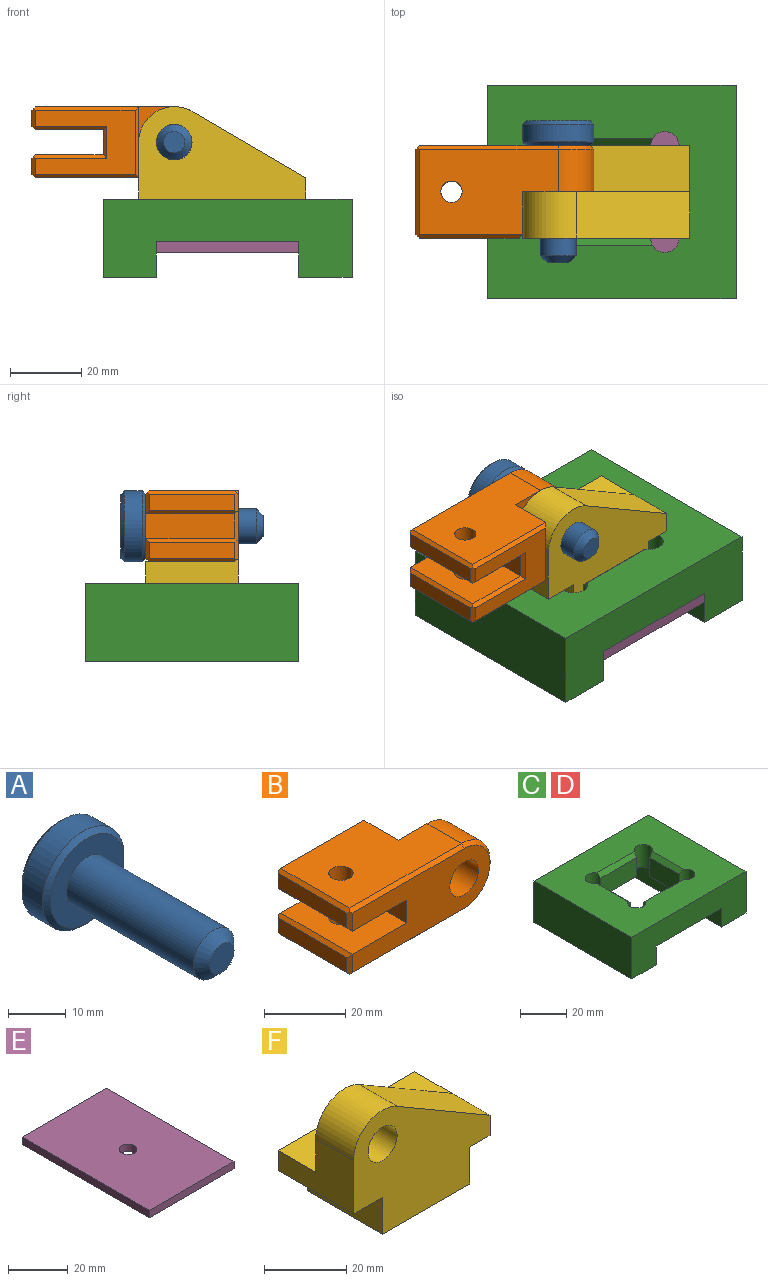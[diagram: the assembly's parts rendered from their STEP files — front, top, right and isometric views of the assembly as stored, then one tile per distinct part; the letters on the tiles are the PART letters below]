
ASSEMBLY  parts=6 mates=4
PART A: 8 faces, bbox 20x40x20 mm
  f0: cylinder r=10mm len=20mm, axis (0,1,0), area 314.2mm2, adj f5,f6
  f1: plane 18x18mm, normal (0,-1,0), area 175.9mm2, adj f3,f6
  f2: plane 18x18mm, normal (0,1,0), area 254.5mm2, adj f5
  f3: cylinder r=5mm len=31mm, axis (0,1,0), area 973.9mm2, adj f1,f7
  f4: plane 6x6mm, normal (0,-1,0), area 28.3mm2, adj f7
  f5: cone r=10mm half-angle=45deg, axis (0,-1,0), area 84.4mm2, adj f0,f2
  f6: cone r=9mm half-angle=45deg, axis (0,1,0), area 84.4mm2, adj f0,f1
  f7: cone r=3mm half-angle=45deg, axis (0,1,0), area 71.1mm2, adj f3,f4
PART B: 32 faces, bbox 50x26x20 mm
  f0: plane 39x24mm, normal (0,0,1), area 787.7mm2, adj f8,f12,f16,f21,f22,f23,f27
  f1: plane 39x24mm, normal (0,0,-1), area 787.7mm2, adj f8,f11,f19,f21,f22,f25,f26
  f2: plane 28x18mm, normal (0,1,0), area 324mm2, adj f15,f20,f26,f27,f28,f29,f30,f31
  f3: plane 24x4.5mm, normal (-1,0,0), area 108mm2, adj f13,f14,f15,f16
  f4: plane 25x19mm, normal (0,0,-1), area 446.7mm2, adj f5,f10,f12,f13,f30
  f5: plane 25x7mm, normal (-1,0,0), area 175mm2, adj f4,f6,f10,f31
  f6: plane 25x19mm, normal (0,0,1), area 446.7mm2, adj f5,f10,f11,f18,f29
  f7: plane 24x4.5mm, normal (-1,0,0), area 108mm2, adj f17,f18,f19,f20
  f8: cylinder r=10mm len=20mm, axis (0,1,0), area 377mm2, adj f0,f1,f22,f24
  f9: cylinder r=5mm len=13mm, axis (0,1,0), area 408.4mm2, adj f10,f22
  f10: plane 48x18mm, normal (0,-1,0), area 617.7mm2, adj f4,f5,f6,f9,f14,f17,f23,f24
  f11: cylinder r=3mm len=6.5mm, axis (0,0,-1), area 122.5mm2, adj f1,f6
  f12: cylinder r=3mm len=6.5mm, axis (0,0,-1), area 122.5mm2, adj f0,f4
  f13: plane 25.5x1mm, normal (-0.71,0,-0.71), area 35mm2, adj f3,f4,f14,f15,f30
  f14: plane 6x1mm, normal (-0.71,-0.71,0), area 7.4mm2, adj f3,f10,f13,f16,f23
  f15: plane 5.5x1mm, normal (-0.71,0.71,0), area 7.1mm2, adj f2,f3,f13,f16,f27,f30
  f16: plane 25x1mm, normal (-0.71,0,0.71), area 34.6mm2, adj f0,f3,f14,f15,f23,f27
  f17: plane 6x1mm, normal (-0.71,-0.71,0), area 7.4mm2, adj f7,f10,f18,f19,f25
  f18: plane 25.5x1mm, normal (-0.71,0,0.71), area 35mm2, adj f6,f7,f17,f20,f29
  f19: plane 25x1mm, normal (-0.71,0,-0.71), area 34.6mm2, adj f1,f7,f17,f20,f25,f26
  f20: plane 5.5x1mm, normal (-0.71,0.71,0), area 7.1mm2, adj f2,f7,f18,f19,f26,f29
  f21: plane 20x12mm, normal (1,0,0), area 240mm2, adj f0,f1,f22,f28
  f22: plane 20x20mm, normal (0,1,0), area 278.5mm2, adj f0,f1,f8,f9,f21
  f23: plane 39.5x1mm, normal (0,-0.71,0.71), area 55.5mm2, adj f0,f10,f14,f16,f24
  f24: cone r=9mm half-angle=45deg, axis (0,1,0), area 42.2mm2, adj f8,f10,f23,f25
  f25: plane 39.5x1mm, normal (0,-0.71,-0.71), area 55.5mm2, adj f1,f10,f17,f19,f24
  f26: plane 29.5x1mm, normal (0,0.71,-0.71), area 40.7mm2, adj f1,f2,f19,f20,f28
  f27: plane 29.5x1mm, normal (0,0.71,0.71), area 40.7mm2, adj f0,f2,f15,f16,f28
  f28: plane 20x1mm, normal (0.71,0.71,0), area 26.9mm2, adj f2,f21,f26,f27
  f29: plane 20.5x1mm, normal (0,0.71,0.71), area 27.9mm2, adj f2,f6,f18,f20,f31
  f30: plane 20.5x1mm, normal (0,0.71,-0.71), area 27.9mm2, adj f2,f4,f13,f15,f31
  f31: plane 9x1mm, normal (-0.71,0.71,0), area 11.3mm2, adj f2,f5,f29,f30
PART C: 22 faces, bbox 70x60x22 mm
  f0: plane 60x15mm, normal (0,0,-1), area 900mm2, adj f8,f9,f11,f19
  f1: plane 22x10mm, normal (0,1,0), area 220mm2, adj f2,f10,f16,f21
  f2: cylinder r=4mm len=12mm, axis (0,0,1), area 222.1mm2, adj f1,f3,f14,f16,f17,f21
  f3: plane 18x10mm, normal (1,0,0), area 180mm2, adj f2,f4,f17,f21
  f4: cylinder r=4mm len=12mm, axis (0,0,1), area 222.1mm2, adj f3,f5,f14,f17,f18,f21
  f5: plane 22x10mm, normal (0,-1,0), area 220mm2, adj f4,f6,f18,f21
  f6: cylinder r=4mm len=12mm, axis (0,0,1), area 222.1mm2, adj f5,f7,f14,f15,f18,f21
  f7: plane 18x10mm, normal (-1,0,0), area 180mm2, adj f6,f10,f15,f21
  f8: plane 70x22mm, normal (0,-1,0), area 1140mm2, adj f0,f11,f12,f13,f14,f19,f20,f21
  f9: plane 70x22mm, normal (0,1,0), area 1140mm2, adj f0,f11,f12,f13,f14,f19,f20,f21
  f10: cylinder r=4mm len=12mm, axis (0,0,1), area 222.1mm2, adj f1,f7,f14,f15,f16,f21
  f11: plane 60x22mm, normal (1,0,0), area 1320mm2, adj f0,f8,f9,f14
  f12: plane 60x22mm, normal (-1,0,0), area 1320mm2, adj f8,f9,f13,f14
  f13: plane 60x15mm, normal (0,0,-1), area 900mm2, adj f8,f9,f12,f20
  f14: plane 70x60mm, normal (0,0,1), area 3106.4mm2, adj f2,f4,f6,f8,f9,f10,f11,f12
  f15: plane 19.07x2mm, normal (-0.71,0,0.71), area 51.9mm2, adj f6,f7,f10,f14
  f16: plane 23.07x2mm, normal (0,0.71,0.71), area 63.2mm2, adj f1,f2,f10,f14
  f17: plane 19.07x2mm, normal (0.71,0,0.71), area 51.9mm2, adj f2,f3,f4,f14
  f18: plane 23.07x2mm, normal (0,-0.71,0.71), area 63.2mm2, adj f4,f5,f6,f14
  f19: plane 60x10mm, normal (-1,0,0), area 600mm2, adj f0,f8,f9,f21
  f20: plane 60x10mm, normal (1,0,0), area 600mm2, adj f8,f9,f13,f21
  f21: plane 60x40mm, normal (0,0,-1), area 1469.2mm2, adj f1,f2,f3,f4,f5,f6,f7,f8
PART D: same geometry as C
PART E: 7 faces, bbox 40x60x3 mm
  f0: plane 40x3mm, normal (0,1,0), area 120mm2, adj f1,f3,f5,f6
  f1: plane 60x3mm, normal (-1,0,0), area 180mm2, adj f0,f2,f5,f6
  f2: plane 40x3mm, normal (0,-1,0), area 120mm2, adj f1,f3,f5,f6
  f3: plane 60x3mm, normal (1,0,0), area 180mm2, adj f0,f2,f5,f6
  f4: cylinder r=3mm len=6mm, axis (0,0,1), area 56.5mm2, adj f5,f6
  f5: plane 60x40mm, normal (0,0,-1), area 2371.7mm2, adj f0,f1,f2,f3,f4
  f6: plane 60x40mm, normal (0,0,1), area 2371.7mm2, adj f0,f1,f2,f3,f4
PART F: 14 faces, bbox 47x26x37 mm
  f0: plane 31.96x18.64mm, normal (0.5,0,0.86), area 481mm2, adj f1,f10,f11,f13
  f1: cylinder r=10mm len=15.04mm, axis (0,-1,0), area 272.8mm2, adj f0,f4,f11,f13
  f2: cylinder r=5mm len=13mm, axis (0,-1,0), area 408.4mm2, adj f11,f13
  f3: plane 47x17mm, normal (0,1,0), area 612mm2, adj f4,f5,f6,f7,f8,f9,f10,f12
  f4: plane 26x16mm, normal (-1,0,0), area 286mm2, adj f1,f3,f5,f11,f12,f13
  f5: plane 26x10mm, normal (0,0,-1), area 260mm2, adj f3,f4,f6,f11
  f6: plane 26x11mm, normal (-1,0,0), area 286mm2, adj f3,f5,f7,f11
  f7: plane 30x26mm, normal (0,0,-1), area 780mm2, adj f3,f6,f8,f11
  f8: plane 26x11mm, normal (1,0,0), area 286mm2, adj f3,f7,f9,f11
  f9: plane 26x7mm, normal (0,0,-1), area 182mm2, adj f3,f8,f10,f11
  f10: plane 26x6mm, normal (1,0,0), area 156mm2, adj f0,f3,f9,f11,f12
  f11: plane 47x37mm, normal (0,-1,0), area 1108.4mm2, adj f0,f1,f2,f4,f5,f6,f7,f8
  f12: plane 47x13mm, normal (0,0,1), area 611mm2, adj f3,f4,f10,f13
  f13: plane 47x20mm, normal (0,1,0), area 496.4mm2, adj f0,f1,f2,f4,f12
PLACE A rot(axis=(0,-1,0),90deg) t=(-15,20,16)mm
PLACE B rot(axis=(1,0,0),180deg) t=(-15,-13,16)mm
PLACE C at identity fixed
PLACE D at identity
PLACE E t=(0,0,-12)mm
PLACE F t=(-1.5,-13,-11)mm
MATE fastened F.f11 <-> C.f1  axis (0,-1,0) through (0,-13,-11)mm
MATE fastened E.f2 <-> C.f8  axis (0,-1,0) through (0,-30,-12)mm
MATE fastened A.f0 <-> B.f9  axis (0,-1,0) through (-15,13,16)mm
MATE revolute B.f9 <-> F.f1  axis (0,-1,0) through (-15,0,16)mm
